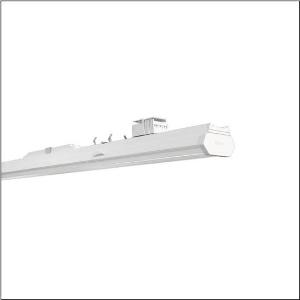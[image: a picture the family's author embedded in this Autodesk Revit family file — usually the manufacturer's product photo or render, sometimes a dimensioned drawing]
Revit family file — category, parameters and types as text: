
# Revit family: licross_21_protected_ho_52tp12dn4e5m3s
name_source: partatom
category: Lighting Fixtures
units: mm (PartAtom-declared; Revit-internal decimal feet)

## family parameters
Cut with Voids When Loaded = No
Host = Face
Light Source = No
Part Type = Normal
Room Calculation Point = No
Round Connector Dimension = Use Diameter
Shared = No

## types (1)
- --- (1 x LED, 910 lm, 7.6 W, 4000K)
    Apparent Load = 8 VA
    CIE Flux Codes = 70 91 97 98 100
    Color Rendering = 80
    Color Temperature = 4000K
    Default Elevation = 1800 mm
    Description = Licross 21 Protected HO, luminaire insert, of sheet steel, galvanised, coil coated, white, length: 1.500mm, width: 90mm, height: 103mm, LED rated luminous flux: 14.690lm, light colour: 840, SDCM (Standard Deviation of Colour Matching)MacAdam ≤ 3 SDCM (initial), control gear: DALI 2 (for two DALI lines), with plug, 6-pole, with phase selection, for trunking rail, 14-core, mains connection: 220..240V, AC, 50/60Hz, rated input power: 89W, for trunking rail, 14-core, internal wiring halogen-free, for emergency light function, converter,control gear: single battery element, battery: LiFePO4, 9Ah, primary light control with lens, of plastic, primary optical cover: cover, of PMMA, light emission: direct distribution, primary light characteristic: symmetric, protection rating (complete): IP64, insulation class (complete): insulation class I (protective earthing), certification: CE, UKCA, protection symbol: D if used in an environment with conductive dust loads with corresponding accessories, impact resistance: IK06, permissible ambient temperature for indoor applications: +5..+30°C, standard: EN 60598-2-22, LABS conformity tested according to VDMA 24364:2018-05, reducing of maximum allowable ambient temperature of 5°C with ceiling mounting, corresponds to IFS (International Featured Standards) requirements for safety and quality in the food industry, The light source and the operating device comply with the requirements of the Ecodesign Regulation (EU) 2019/2020 and are replaceable in accordance with this regulation, packaging unit: 1 piece
    Height = 92 mm
    Lamp = 1 x LED
    Lamp Light Flux = 910 lm
    Lamp Power = 7.6 W
    Lamp count = 1
    Length = 1500 mm
    Luminous efficacy = 120 lm/W
    Manufacturer = Siteco
    ModVariant = No
    Model = 52TP12DN4E5M3S
    Mounting Place = Ceiling
    Mounting Type = Pendant
    Number of Poles = 1
    OnlyDefault = Yes
    Power Factor = 1
    Product Name = Licross 21 Protected HO
    Product group = luminaire insert | ceiling pendant
    ProductGroupID = 901
    Protection Class = Protection class I
    Protection Degree = IP 64
    RLX_Detail_Level = 1
    RLX_Emergency_Light_Flux = 0 lm
    RLX_Emergency_Type = 0
    RLX_Emergency_Type_DB = No
    RlxData = <blob elided: 25165 chars, md5=cf34c52f>
    Socket = socket
    Standby Power = 0 W
    System Light Flux = 910 lm
    System Power = 8 W
    Type Comments = : emergency light operation: 3 h
    Type Image = l_1256148.jpg
    URL = http://relux.com
    VarID = @adj_112733
    Voltage = 0 V
    Weight = 0.00 kg
    Width = 88 mm

## geometry (parser evidence)
native form markers: Blend x4, Sweep x10
no freeform markers — native parametric forms only
